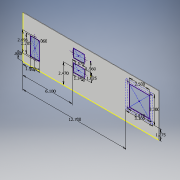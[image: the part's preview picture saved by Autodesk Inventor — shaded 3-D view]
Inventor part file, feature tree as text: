
AUTODESK INVENTOR PART (.ipt)
format: ipt  version: 2017 (Build 210142000, 142)  size: 189,952 bytes
history: native  units: in
note: dims shown in document units (in); Inventor stores cm internally (conversion verified against a paired STEP export)
features: extrude x4, other x3, hole x3, fillet x2, sketch x1
ambient origin geometry x8: Origin, YZ Plane, XZ Plane, XY Plane, X Axis, Y Axis, Z Axis, Center Point
bodies: Solid1 (feature_tree)
feature tree (13):
  extrude  "PDU back"  Depth=5.22in
  other  "pwr entry"
  extrude  "pwr entry cutout"  Depth=0.065in TaperAngle=0.0deg
  hole  "pwr entry holes"  [1 undecoded]
  other  "IEC outlet"
  hole  "IEC holes"  [1 undecoded]
  extrude  "IEC cutout"  Depth=0.196in
  other  "airflow"
  hole  "airflow holes"  [1 undecoded]
  extrude  "airflow cutout"  Depth=0.196in
  fillet  "IEC fillet 1"  Radius=0.06in
  fillet  "IEC fillet 2"  [1 undecoded]
  sketch  "Sketch1"  dims[d0=16.73in d1=5.22in d2=0.065in d3=0.0in d4=2.205in d5=1.124in d6=2.496in d7=1.5in d8=0.8795in d9=0.06in d10=0.0in d11=0.0in d12=0.136in d13=0.75in d14=0.375in d15=0.25in d16=0.5635in d17=1.0in d18=0.8108in d19=1.025in d20=1.345in d22=1.575in d23=6.1in d24=2.47in d25=0.7874in d27=1.56in d28=0.3937in d30=1.0in d34=0.136in d35=0.75in d36=0.375in d37=0.25in d38=0.5635in d39=1.0in d40=0.8108in d41=1.0in d42=0.0in d43=3.3in d44=3.3in d45=12.7in d46=1.275in d47=2.5in d48=2.81in d49=0.177in d50=0.75in d51=0.375in d52=0.25in d53=0.5635in d54=1.0in d55=0.8108in d56=1.0in d57=0.0in d58=0.196in d59=0.196in]
note: 4 required parameter values undecoded (feature->parameter linkage not recoverable at this tier; creation-order binding heuristic only, values carry confidence <= 0.55)
